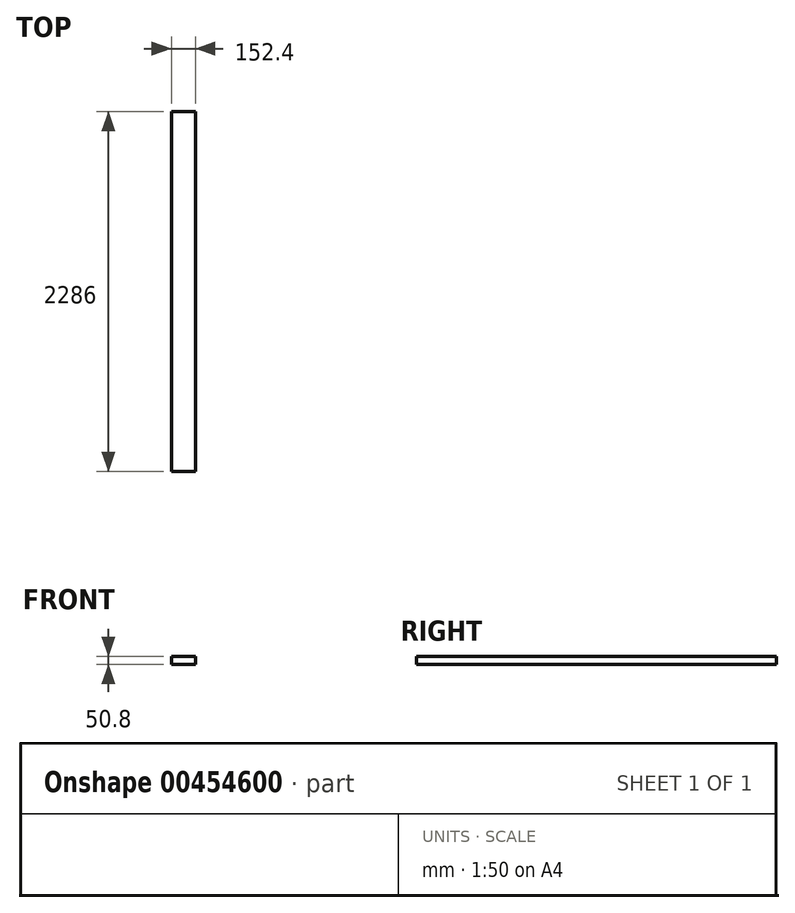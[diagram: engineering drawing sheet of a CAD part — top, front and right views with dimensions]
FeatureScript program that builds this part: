
annotation { "Feature Type Name" : "Feature", "Feature Type Description" : "" }
export const myFeature = defineFeature(function(context is Context, id is Id, definition is map)
    precondition{}
    {
        {
            var Q0;
            Q0=qCreatedBy(makeId("Front.planeOp"),FACE);
            var sketch = newSketch(context, id + "F0", { "sketchPlane" : qUnion([Q0])});
            skLineSegment(sketch, "E0.bottom", {"start": v(76.2, 25.4) * mm, "end": v(-76.2, 25.4) * mm});
            skLineSegment(sketch, "E0.top", {"start": v(76.2, -25.4) * mm, "end": v(-76.2, -25.4) * mm});
            skLineSegment(sketch, "E0.left", {"start": v(76.2, 25.4) * mm, "end": v(76.2, -25.4) * mm});
            skLineSegment(sketch, "E0.right", {"start": v(-76.2, 25.4) * mm, "end": v(-76.2, -25.4) * mm});
            skPoint(sketch, "E0.middle", {"position": v(0, 0) * mm});
            skSolve(sketch);
        }
        {
            var Q0;
            Q0=makeQuery(id+"F0.imprint","IMPRINT",FACE,{"disambiguationData":[TD([[makeQuery(id+"F0.imprint","IMPRINT",EDGE,{"derivedFrom":sQuery(id+"F0.wireOp",EDGE,"E0.bottom")}),1.0]])]});
            extrude(context, id + "F1", {"entities" : qUnion([Q0]), "depth" : 2286 * mm});
        }
    });
